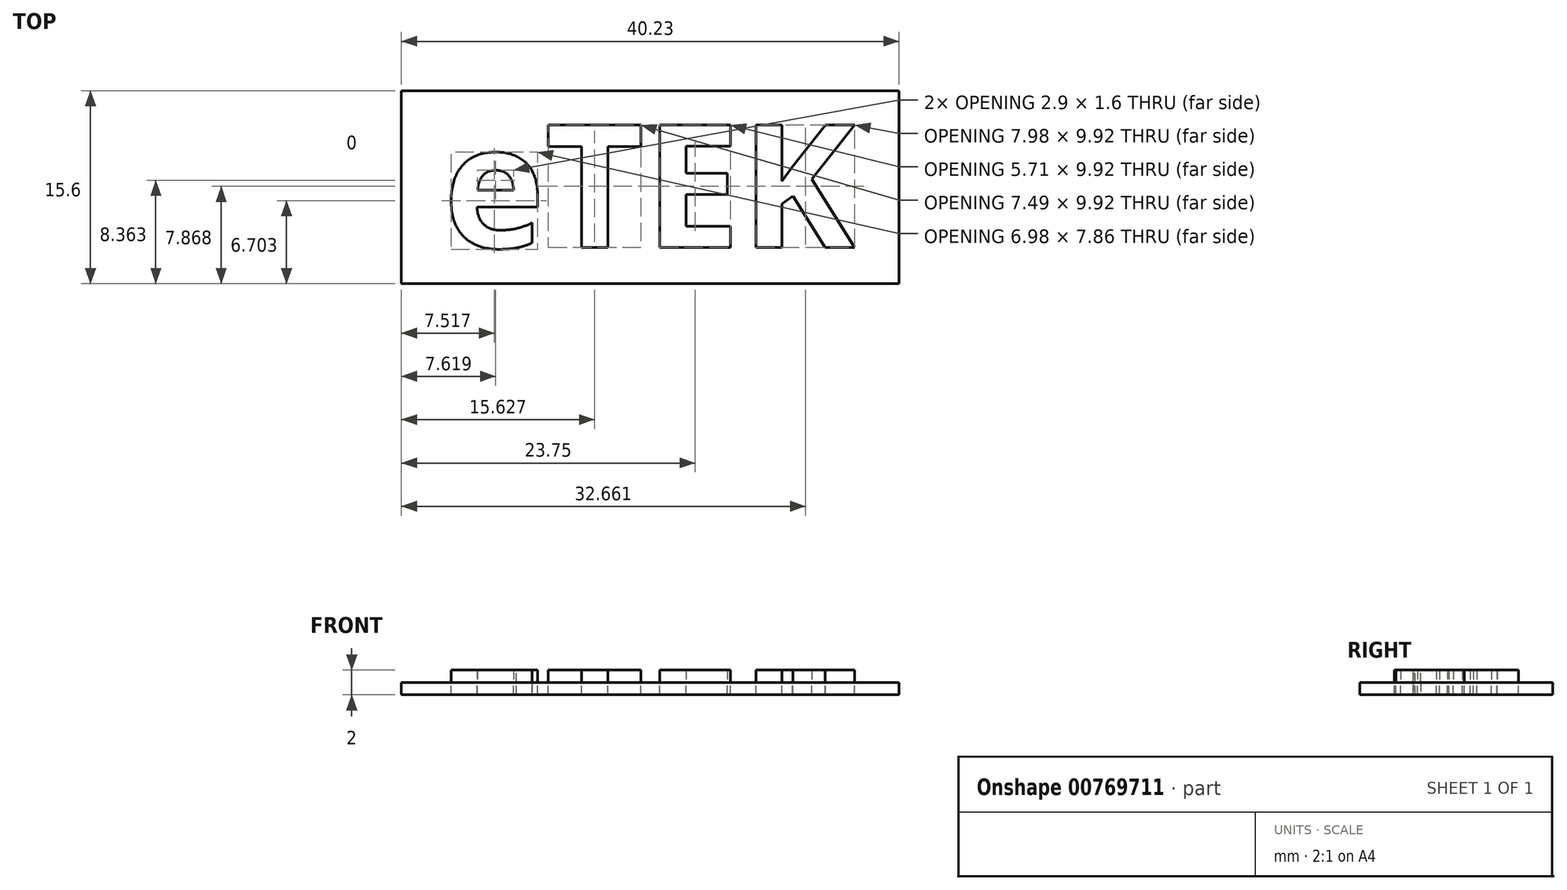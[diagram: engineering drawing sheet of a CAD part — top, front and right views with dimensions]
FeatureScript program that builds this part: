
annotation { "Feature Type Name" : "Feature", "Feature Type Description" : "" }
export const myFeature = defineFeature(function(context is Context, id is Id, definition is map)
    precondition{}
    {
        {
            var Q0;
            Q0=qCreatedBy(makeId("Top.planeOp"),FACE);
            var sketch = newSketch(context, id + "F0", { "sketchPlane" : qUnion([Q0])});
            skText(sketch, "E0", { "text": "eTEK", "fontName": "OpenSans-Bold.ttf"});
            skLineSegment(sketch, "E1.bottom", {"start": v(-3.4, 2.69) * mm, "end": v(36.83, 2.69) * mm});
            skLineSegment(sketch, "E1.top", {"start": v(-3.4, -12.9) * mm, "end": v(36.83, -12.9) * mm});
            skLineSegment(sketch, "E1.left", {"start": v(-3.4, 2.69) * mm, "end": v(-3.4, -12.9) * mm});
            skLineSegment(sketch, "E1.right", {"start": v(36.83, 2.69) * mm, "end": v(36.83, -12.9) * mm});
            const initialGuessF0  = {"E0": [0, -0.01, 1, 0, 0.01]};
            skSetInitialGuess(sketch, initialGuessF0);
            skSolve(sketch);
        }
        {
            var Q0;
            Q0=makeQuery(id+"F0.imprint","IMPRINT",FACE,{"disambiguationData":[TD([[makeQuery(id+"F0.imprint","IMPRINT",EDGE,{"derivedFrom":sQuery(id+"F0.wireOp",EDGE,"E0.sketch_text.stroke-0")}),-1.0]])]});
            var Q1;
            Q1=makeQuery(id+"F0.imprint","IMPRINT",FACE,{"disambiguationData":[TD([[makeQuery(id+"F0.imprint","IMPRINT",EDGE,{"derivedFrom":sQuery(id+"F0.wireOp",EDGE,"E0.sketch_text.stroke-20")}),-1.0]])]});
            var Q2;
            Q2=makeQuery(id+"F0.imprint","IMPRINT",FACE,{"disambiguationData":[TD([[makeQuery(id+"F0.imprint","IMPRINT",EDGE,{"derivedFrom":sQuery(id+"F0.wireOp",EDGE,"E0.sketch_text.stroke-28")}),-1.0]])]});
            var Q3;
            Q3=makeQuery(id+"F0.imprint","IMPRINT",FACE,{"disambiguationData":[TD([[makeQuery(id+"F0.imprint","IMPRINT",EDGE,{"derivedFrom":sQuery(id+"F0.wireOp",EDGE,"E0.sketch_text.stroke-40")}),-1.0]])]});
            extrude(context, id + "F1", {"entities" : qUnion([Q0, Q1, Q2, Q3]), "depth" : 1 * mm, "offsetDistance" : 25 * mm});
        }
        {
            var Q0;
            Q0=makeQuery(id+"F0.imprint","IMPRINT",FACE,{"disambiguationData":[TD([[makeQuery(id+"F0.imprint","IMPRINT",EDGE,{"derivedFrom":sQuery(id+"F0.wireOp",EDGE,"E0.sketch_text.stroke-5")}),1.0]])]});
            extrude(context, id + "F2", {"entities" : qUnion([Q0]), "depth" : -1 * mm, "offsetDistance" : 25 * mm});
        }
        {
            var Q0;
            Q0=makeQuery(id+"F0.imprint","IMPRINT",FACE,{"disambiguationData":[TD([[makeQuery(id+"F0.imprint","IMPRINT",EDGE,{"derivedFrom":sQuery(id+"F0.wireOp",EDGE,"E0.sketch_text.stroke-40")}),-1.0]])]});
            var Q1;
            Q1=makeQuery(id+"F0.imprint","IMPRINT",FACE,{"disambiguationData":[TD([[makeQuery(id+"F0.imprint","IMPRINT",EDGE,{"derivedFrom":sQuery(id+"F0.wireOp",EDGE,"E0.sketch_text.stroke-28")}),-1.0]])]});
            var Q2;
            Q2=makeQuery(id+"F0.imprint","IMPRINT",FACE,{"disambiguationData":[TD([[makeQuery(id+"F0.imprint","IMPRINT",EDGE,{"derivedFrom":sQuery(id+"F0.wireOp",EDGE,"E0.sketch_text.stroke-20")}),-1.0]])]});
            var Q3;
            Q3=makeQuery(id+"F0.imprint","IMPRINT",FACE,{"disambiguationData":[TD([[makeQuery(id+"F0.imprint","IMPRINT",EDGE,{"derivedFrom":sQuery(id+"F0.wireOp",EDGE,"E0.sketch_text.stroke-0")}),-1.0]])]});
            extrude(context, id + "F3", {"entities" : qUnion([Q0, Q1, Q2, Q3]), "depth" : -1 * mm, "offsetDistance" : 25 * mm});
        }
    });
